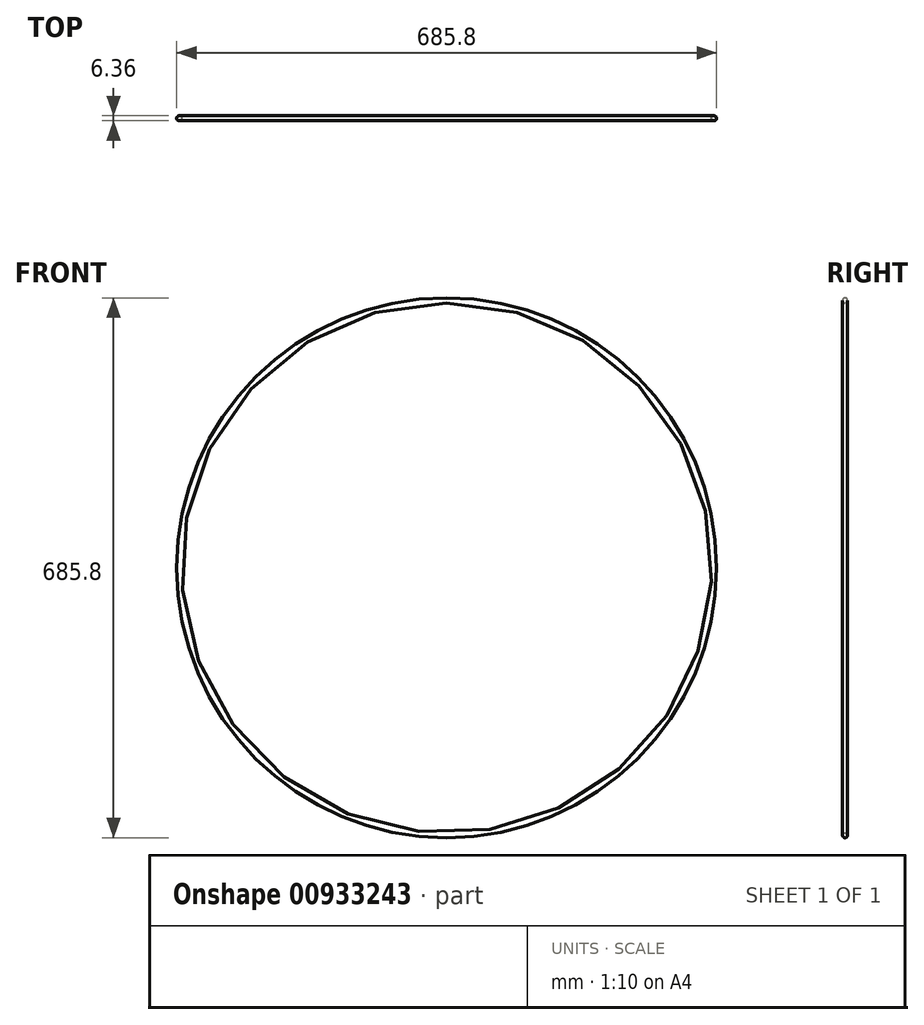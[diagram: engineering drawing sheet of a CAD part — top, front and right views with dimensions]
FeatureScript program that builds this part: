
annotation { "Feature Type Name" : "Feature", "Feature Type Description" : "" }
export const myFeature = defineFeature(function(context is Context, id is Id, definition is map)
    precondition{}
    {
        {
            var Q0;
            Q0=qCreatedBy(makeId("Front.planeOp"),FACE);
            var sketch = newSketch(context, id + "F0", { "sketchPlane" : qUnion([Q0])});
            skCircle(sketch, "E0", {"center": v(0, 0) * mm, "radius": 339.73 * mm});
            skSolve(sketch);
        }
        {
            var Q0;
            Q0=qCreatedBy(makeId("Right.planeOp"),FACE);
            var sketch = newSketch(context, id + "F1", { "sketchPlane" : qUnion([Q0])});
            skCircle(sketch, "E1", {"center": v(0, 339.73) * mm, "radius": 3.18 * mm});
            skSolve(sketch);
        }
        {
            var Q0;
            Q0 = qSketchRegion(id + "F1", true);
            var Q1;
            Q1=sQuery(id+"F0.wireOp",EDGE,"E0");
            revolve(context, id + "F2", {"surfaceOperationType" : NewSurfaceOperationType.NEW, "entities" : qUnion([Q0]), "axis" : qUnion([Q1]), "revolveType" : RevolveType.FULL});
        }
    });
